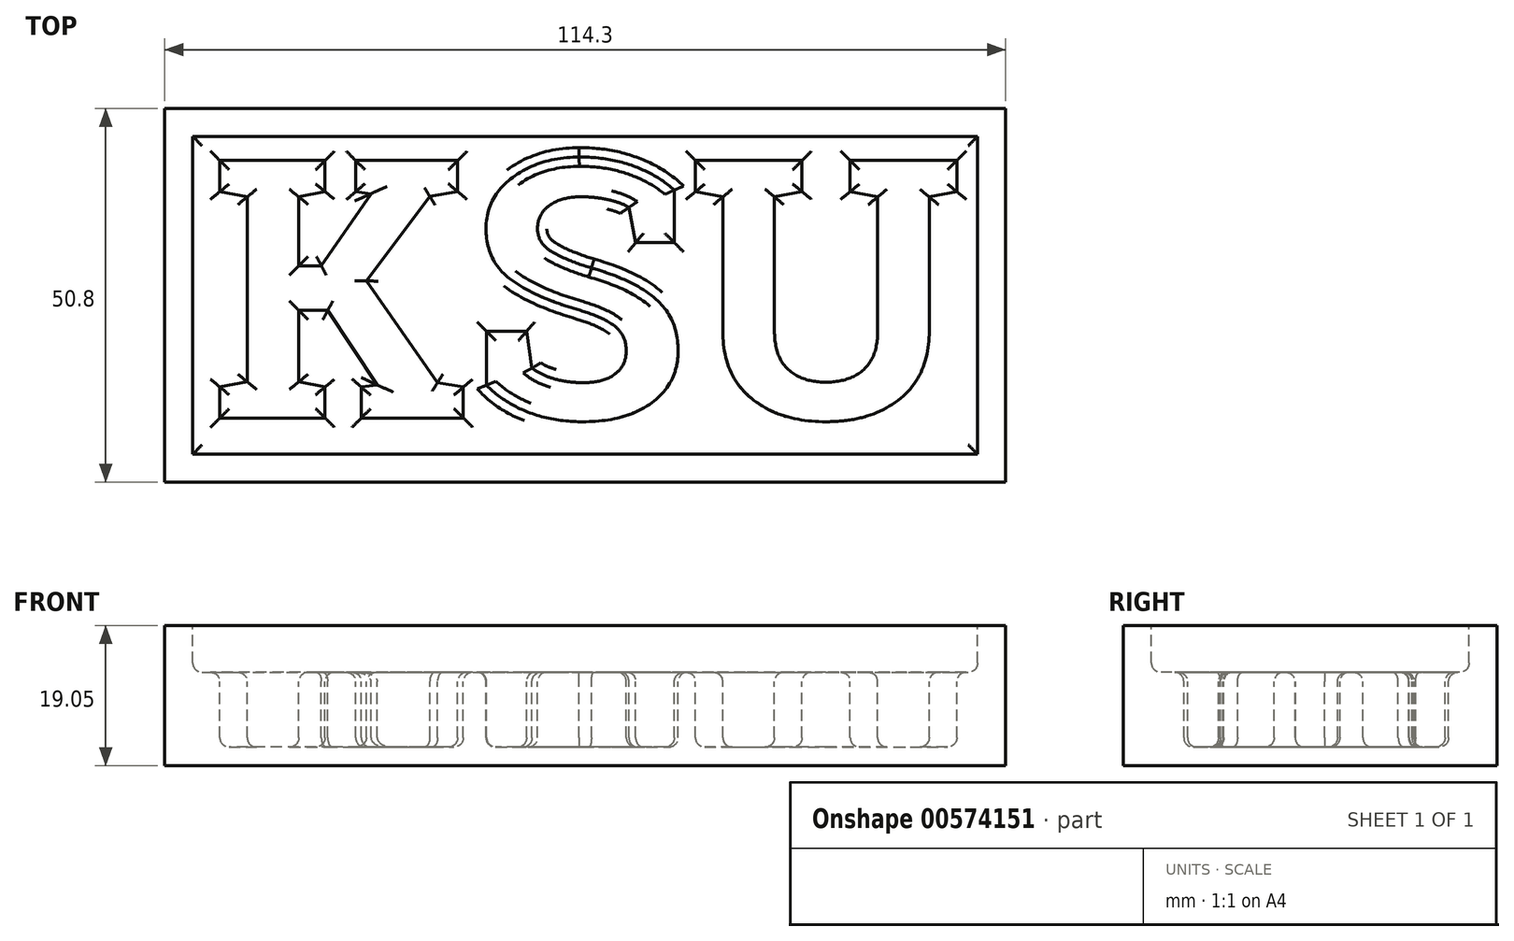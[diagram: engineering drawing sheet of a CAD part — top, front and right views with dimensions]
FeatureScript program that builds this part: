
annotation { "Feature Type Name" : "Feature", "Feature Type Description" : "" }
export const myFeature = defineFeature(function(context is Context, id is Id, definition is map)
    precondition{}
    {
        {
            var Q0;
            Q0=qCreatedBy(makeId("Top.planeOp"),FACE);
            var sketch = newSketch(context, id + "F0", { "sketchPlane" : qUnion([Q0])});
            skLineSegment(sketch, "E0.bottom", {"start": v(-40.64, 25.4) * mm, "end": v(73.66, 25.4) * mm});
            skLineSegment(sketch, "E0.top", {"start": v(-40.64, -25.4) * mm, "end": v(73.66, -25.4) * mm});
            skLineSegment(sketch, "E0.left", {"start": v(-40.64, 25.4) * mm, "end": v(-40.64, -25.4) * mm});
            skLineSegment(sketch, "E0.right", {"start": v(73.66, 25.4) * mm, "end": v(73.66, -25.4) * mm});
            skSolve(sketch);
        }
        {
            var Q0;
            Q0=makeQuery(id+"F0.imprint","IMPRINT",FACE,{"disambiguationData":[TD([[makeQuery(id+"F0.imprint","IMPRINT",EDGE,{"derivedFrom":sQuery(id+"F0.wireOp",EDGE,"E0.bottom")}),-1.0]])]});
            extrude(context, id + "F1", {"entities" : qUnion([Q0]), "depth" : 19.05 * mm, "offsetDistance" : 25.4 * mm});
        }
        {
            var Q0;
            Q0=makeQuery(id+"F1.opExtrude","CAP_FACE",FACE,{"disambiguationData":[OSD([sQuery(id+"F0.wireOp",EDGE,"E0.bottom"),sQuery(id+"F0.wireOp",EDGE,"E0.top"),sQuery(id+"F0.wireOp",EDGE,"E0.left"),sQuery(id+"F0.wireOp",EDGE,"E0.right")])],"isStart":false});
            var sketch = newSketch(context, id + "F2", { "sketchPlane" : qUnion([Q0])});
            skText(sketch, "E1", { "text": "KSU", "fontName": "RobotoSlab-Bold.ttf"});
            const initialGuessF2  = {"E1": [-0.0345, -0.01668, 1, 0, 0.03545]};
            skSetInitialGuess(sketch, initialGuessF2);
            skSolve(sketch);
        }
        {
            var Q0;
            Q0=makeQuery(id+"F2.imprint","IMPRINT",FACE,{"disambiguationData":[TD([[makeQuery(id+"F2.imprint","IMPRINT",EDGE,{"derivedFrom":sQuery(id+"F2.wireOp",EDGE,"E1.sketch_text.stroke-0")}),-1.0]])]});
            var Q1;
            Q1=makeQuery(id+"F2.imprint","IMPRINT",FACE,{"disambiguationData":[TD([[makeQuery(id+"F2.imprint","IMPRINT",EDGE,{"derivedFrom":sQuery(id+"F2.wireOp",EDGE,"E1.sketch_text.stroke-29")}),-1.0]])]});
            var Q2;
            Q2=makeQuery(id+"F2.imprint","IMPRINT",FACE,{"disambiguationData":[TD([[makeQuery(id+"F2.imprint","IMPRINT",EDGE,{"derivedFrom":sQuery(id+"F2.wireOp",EDGE,"E1.sketch_text.stroke-59")}),-1.0]])]});
            extrude(context, id + "F3", {"entities" : qUnion([Q0, Q1, Q2]), "operationType" : NewBodyOperationType.REMOVE, "oppositeDirection" : true, "depth" : 16.5 * mm, "offsetDistance" : 25.4 * mm});
        }
        {
            var Q0;
            Q0=makeQuery(id+"F1.opExtrude","CAP_FACE",FACE,{"disambiguationData":[OSD([sQuery(id+"F0.wireOp",EDGE,"E0.bottom"),sQuery(id+"F0.wireOp",EDGE,"E0.top"),sQuery(id+"F0.wireOp",EDGE,"E0.left"),sQuery(id+"F0.wireOp",EDGE,"E0.right")])],"isStart":false});
            var sketch = newSketch(context, id + "F4", { "sketchPlane" : qUnion([Q0])});
            skLineSegment(sketch, "E2.bottom", {"start": v(-36.83, 21.59) * mm, "end": v(69.85, 21.59) * mm});
            skLineSegment(sketch, "E2.top", {"start": v(-36.83, -21.59) * mm, "end": v(69.85, -21.59) * mm});
            skLineSegment(sketch, "E2.left", {"start": v(-36.83, 21.59) * mm, "end": v(-36.83, -21.59) * mm});
            skLineSegment(sketch, "E2.right", {"start": v(69.85, 21.59) * mm, "end": v(69.85, -21.59) * mm});
            skSolve(sketch);
        }
        {
            var Q0;
            Q0=makeQuery(id+"F4.imprint","IMPRINT",FACE,{"disambiguationData":[TD([[makeQuery(id+"F4.imprint","IMPRINT",EDGE,{"derivedFrom":sQuery(id+"F4.wireOp",EDGE,"E2.bottom")}),-1.0]])]});
            extrude(context, id + "F5", {"entities" : qUnion([Q0]), "operationType" : NewBodyOperationType.REMOVE, "oppositeDirection" : true, "depth" : 6.35 * mm, "offsetDistance" : 25.4 * mm});
        }
        {
            var Q0;
            Q0=makeQuery(id+"F3.boolean.opBoolean","COPY",FACE,{"derivedFrom":makeQuery(id+"F3.opExtrude","CAP_FACE",FACE,{"disambiguationData":[OSD([sQuery(id+"F2.wireOp",EDGE,"E1.sketch_text.stroke-0"),sQuery(id+"F2.wireOp",EDGE,"E1.sketch_text.stroke-1"),sQuery(id+"F2.wireOp",EDGE,"E1.sketch_text.stroke-2"),sQuery(id+"F2.wireOp",EDGE,"E1.sketch_text.stroke-3"),sQuery(id+"F2.wireOp",EDGE,"E1.sketch_text.stroke-4"),sQuery(id+"F2.wireOp",EDGE,"E1.sketch_text.stroke-5"),sQuery(id+"F2.wireOp",EDGE,"E1.sketch_text.stroke-6"),sQuery(id+"F2.wireOp",EDGE,"E1.sketch_text.stroke-7"),sQuery(id+"F2.wireOp",EDGE,"E1.sketch_text.stroke-8"),sQuery(id+"F2.wireOp",EDGE,"E1.sketch_text.stroke-9"),sQuery(id+"F2.wireOp",EDGE,"E1.sketch_text.stroke-10"),sQuery(id+"F2.wireOp",EDGE,"E1.sketch_text.stroke-11"),sQuery(id+"F2.wireOp",EDGE,"E1.sketch_text.stroke-12"),sQuery(id+"F2.wireOp",EDGE,"E1.sketch_text.stroke-13"),sQuery(id+"F2.wireOp",EDGE,"E1.sketch_text.stroke-14"),sQuery(id+"F2.wireOp",EDGE,"E1.sketch_text.stroke-15"),sQuery(id+"F2.wireOp",EDGE,"E1.sketch_text.stroke-16"),sQuery(id+"F2.wireOp",EDGE,"E1.sketch_text.stroke-17"),sQuery(id+"F2.wireOp",EDGE,"E1.sketch_text.stroke-18"),sQuery(id+"F2.wireOp",EDGE,"E1.sketch_text.stroke-19"),sQuery(id+"F2.wireOp",EDGE,"E1.sketch_text.stroke-20"),sQuery(id+"F2.wireOp",EDGE,"E1.sketch_text.stroke-21"),sQuery(id+"F2.wireOp",EDGE,"E1.sketch_text.stroke-22"),sQuery(id+"F2.wireOp",EDGE,"E1.sketch_text.stroke-23"),sQuery(id+"F2.wireOp",EDGE,"E1.sketch_text.stroke-24"),sQuery(id+"F2.wireOp",EDGE,"E1.sketch_text.stroke-25"),sQuery(id+"F2.wireOp",EDGE,"E1.sketch_text.stroke-26"),sQuery(id+"F2.wireOp",EDGE,"E1.sketch_text.stroke-27"),sQuery(id+"F2.wireOp",EDGE,"E1.sketch_text.stroke-28")])],"isStart":false})});
            var Q1;
            Q1=makeQuery(id+"F3.boolean.opBoolean","COPY",FACE,{"derivedFrom":makeQuery(id+"F3.opExtrude","CAP_FACE",FACE,{"disambiguationData":[OSD([sQuery(id+"F2.wireOp",EDGE,"E1.sketch_text.stroke-29"),sQuery(id+"F2.wireOp",EDGE,"E1.sketch_text.stroke-30"),sQuery(id+"F2.wireOp",EDGE,"E1.sketch_text.stroke-31"),sQuery(id+"F2.wireOp",EDGE,"E1.sketch_text.stroke-32"),sQuery(id+"F2.wireOp",EDGE,"E1.sketch_text.stroke-33"),sQuery(id+"F2.wireOp",EDGE,"E1.sketch_text.stroke-34"),sQuery(id+"F2.wireOp",EDGE,"E1.sketch_text.stroke-35"),sQuery(id+"F2.wireOp",EDGE,"E1.sketch_text.stroke-36"),sQuery(id+"F2.wireOp",EDGE,"E1.sketch_text.stroke-37"),sQuery(id+"F2.wireOp",EDGE,"E1.sketch_text.stroke-38"),sQuery(id+"F2.wireOp",EDGE,"E1.sketch_text.stroke-39"),sQuery(id+"F2.wireOp",EDGE,"E1.sketch_text.stroke-40"),sQuery(id+"F2.wireOp",EDGE,"E1.sketch_text.stroke-41"),sQuery(id+"F2.wireOp",EDGE,"E1.sketch_text.stroke-42"),sQuery(id+"F2.wireOp",EDGE,"E1.sketch_text.stroke-43"),sQuery(id+"F2.wireOp",EDGE,"E1.sketch_text.stroke-44"),sQuery(id+"F2.wireOp",EDGE,"E1.sketch_text.stroke-45"),sQuery(id+"F2.wireOp",EDGE,"E1.sketch_text.stroke-46"),sQuery(id+"F2.wireOp",EDGE,"E1.sketch_text.stroke-47"),sQuery(id+"F2.wireOp",EDGE,"E1.sketch_text.stroke-48"),sQuery(id+"F2.wireOp",EDGE,"E1.sketch_text.stroke-49"),sQuery(id+"F2.wireOp",EDGE,"E1.sketch_text.stroke-50"),sQuery(id+"F2.wireOp",EDGE,"E1.sketch_text.stroke-51"),sQuery(id+"F2.wireOp",EDGE,"E1.sketch_text.stroke-52"),sQuery(id+"F2.wireOp",EDGE,"E1.sketch_text.stroke-53"),sQuery(id+"F2.wireOp",EDGE,"E1.sketch_text.stroke-54"),sQuery(id+"F2.wireOp",EDGE,"E1.sketch_text.stroke-55"),sQuery(id+"F2.wireOp",EDGE,"E1.sketch_text.stroke-56"),sQuery(id+"F2.wireOp",EDGE,"E1.sketch_text.stroke-57"),sQuery(id+"F2.wireOp",EDGE,"E1.sketch_text.stroke-58")])],"isStart":false})});
            var Q2;
            Q2=makeQuery(id+"F3.boolean.opBoolean","COPY",FACE,{"derivedFrom":makeQuery(id+"F3.opExtrude","CAP_FACE",FACE,{"disambiguationData":[OSD([sQuery(id+"F2.wireOp",EDGE,"E1.sketch_text.stroke-59"),sQuery(id+"F2.wireOp",EDGE,"E1.sketch_text.stroke-60"),sQuery(id+"F2.wireOp",EDGE,"E1.sketch_text.stroke-61"),sQuery(id+"F2.wireOp",EDGE,"E1.sketch_text.stroke-62"),sQuery(id+"F2.wireOp",EDGE,"E1.sketch_text.stroke-63"),sQuery(id+"F2.wireOp",EDGE,"E1.sketch_text.stroke-64"),sQuery(id+"F2.wireOp",EDGE,"E1.sketch_text.stroke-65"),sQuery(id+"F2.wireOp",EDGE,"E1.sketch_text.stroke-66"),sQuery(id+"F2.wireOp",EDGE,"E1.sketch_text.stroke-67"),sQuery(id+"F2.wireOp",EDGE,"E1.sketch_text.stroke-68"),sQuery(id+"F2.wireOp",EDGE,"E1.sketch_text.stroke-69"),sQuery(id+"F2.wireOp",EDGE,"E1.sketch_text.stroke-70"),sQuery(id+"F2.wireOp",EDGE,"E1.sketch_text.stroke-71"),sQuery(id+"F2.wireOp",EDGE,"E1.sketch_text.stroke-72"),sQuery(id+"F2.wireOp",EDGE,"E1.sketch_text.stroke-73"),sQuery(id+"F2.wireOp",EDGE,"E1.sketch_text.stroke-74"),sQuery(id+"F2.wireOp",EDGE,"E1.sketch_text.stroke-75"),sQuery(id+"F2.wireOp",EDGE,"E1.sketch_text.stroke-76"),sQuery(id+"F2.wireOp",EDGE,"E1.sketch_text.stroke-77"),sQuery(id+"F2.wireOp",EDGE,"E1.sketch_text.stroke-78"),sQuery(id+"F2.wireOp",EDGE,"E1.sketch_text.stroke-79"),sQuery(id+"F2.wireOp",EDGE,"E1.sketch_text.stroke-80"),sQuery(id+"F2.wireOp",EDGE,"E1.sketch_text.stroke-81"),sQuery(id+"F2.wireOp",EDGE,"E1.sketch_text.stroke-82")])],"isStart":false})});
            fillet(context, id + "F6", {"entities" : qUnion([Q0, Q1, Q2]), "radius" : 1.27 * mm, "tangentPropagation" : true, "allowEdgeOverflow" : false});
        }
        {
            var Q0;
            Q0=makeQuery(id+"F5.boolean.opBoolean","COPY",FACE,{"derivedFrom":makeQuery(id+"F5.opExtrude","CAP_FACE",FACE,{"disambiguationData":[OSD([sQuery(id+"F2.wireOp",EDGE,"E1.sketch_text.stroke-0"),sQuery(id+"F2.wireOp",EDGE,"E1.sketch_text.stroke-1"),sQuery(id+"F2.wireOp",EDGE,"E1.sketch_text.stroke-2"),sQuery(id+"F2.wireOp",EDGE,"E1.sketch_text.stroke-3"),sQuery(id+"F2.wireOp",EDGE,"E1.sketch_text.stroke-4"),sQuery(id+"F2.wireOp",EDGE,"E1.sketch_text.stroke-5"),sQuery(id+"F2.wireOp",EDGE,"E1.sketch_text.stroke-6"),sQuery(id+"F2.wireOp",EDGE,"E1.sketch_text.stroke-7"),sQuery(id+"F2.wireOp",EDGE,"E1.sketch_text.stroke-8"),sQuery(id+"F2.wireOp",EDGE,"E1.sketch_text.stroke-9"),sQuery(id+"F2.wireOp",EDGE,"E1.sketch_text.stroke-10"),sQuery(id+"F2.wireOp",EDGE,"E1.sketch_text.stroke-11"),sQuery(id+"F2.wireOp",EDGE,"E1.sketch_text.stroke-12"),sQuery(id+"F2.wireOp",EDGE,"E1.sketch_text.stroke-13"),sQuery(id+"F2.wireOp",EDGE,"E1.sketch_text.stroke-14"),sQuery(id+"F2.wireOp",EDGE,"E1.sketch_text.stroke-15"),sQuery(id+"F2.wireOp",EDGE,"E1.sketch_text.stroke-16"),sQuery(id+"F2.wireOp",EDGE,"E1.sketch_text.stroke-17"),sQuery(id+"F2.wireOp",EDGE,"E1.sketch_text.stroke-18"),sQuery(id+"F2.wireOp",EDGE,"E1.sketch_text.stroke-19"),sQuery(id+"F2.wireOp",EDGE,"E1.sketch_text.stroke-20"),sQuery(id+"F2.wireOp",EDGE,"E1.sketch_text.stroke-21"),sQuery(id+"F2.wireOp",EDGE,"E1.sketch_text.stroke-22"),sQuery(id+"F2.wireOp",EDGE,"E1.sketch_text.stroke-23"),sQuery(id+"F2.wireOp",EDGE,"E1.sketch_text.stroke-24"),sQuery(id+"F2.wireOp",EDGE,"E1.sketch_text.stroke-25"),sQuery(id+"F2.wireOp",EDGE,"E1.sketch_text.stroke-26"),sQuery(id+"F2.wireOp",EDGE,"E1.sketch_text.stroke-27"),sQuery(id+"F2.wireOp",EDGE,"E1.sketch_text.stroke-28"),sQuery(id+"F2.wireOp",EDGE,"E1.sketch_text.stroke-29"),sQuery(id+"F2.wireOp",EDGE,"E1.sketch_text.stroke-30"),sQuery(id+"F2.wireOp",EDGE,"E1.sketch_text.stroke-31"),sQuery(id+"F2.wireOp",EDGE,"E1.sketch_text.stroke-32"),sQuery(id+"F2.wireOp",EDGE,"E1.sketch_text.stroke-33"),sQuery(id+"F2.wireOp",EDGE,"E1.sketch_text.stroke-34"),sQuery(id+"F2.wireOp",EDGE,"E1.sketch_text.stroke-35"),sQuery(id+"F2.wireOp",EDGE,"E1.sketch_text.stroke-36"),sQuery(id+"F2.wireOp",EDGE,"E1.sketch_text.stroke-37"),sQuery(id+"F2.wireOp",EDGE,"E1.sketch_text.stroke-38"),sQuery(id+"F2.wireOp",EDGE,"E1.sketch_text.stroke-39"),sQuery(id+"F2.wireOp",EDGE,"E1.sketch_text.stroke-40"),sQuery(id+"F2.wireOp",EDGE,"E1.sketch_text.stroke-41"),sQuery(id+"F2.wireOp",EDGE,"E1.sketch_text.stroke-42"),sQuery(id+"F2.wireOp",EDGE,"E1.sketch_text.stroke-43"),sQuery(id+"F2.wireOp",EDGE,"E1.sketch_text.stroke-44"),sQuery(id+"F2.wireOp",EDGE,"E1.sketch_text.stroke-45"),sQuery(id+"F2.wireOp",EDGE,"E1.sketch_text.stroke-46"),sQuery(id+"F2.wireOp",EDGE,"E1.sketch_text.stroke-47"),sQuery(id+"F2.wireOp",EDGE,"E1.sketch_text.stroke-48"),sQuery(id+"F2.wireOp",EDGE,"E1.sketch_text.stroke-49"),sQuery(id+"F2.wireOp",EDGE,"E1.sketch_text.stroke-50"),sQuery(id+"F2.wireOp",EDGE,"E1.sketch_text.stroke-51"),sQuery(id+"F2.wireOp",EDGE,"E1.sketch_text.stroke-52"),sQuery(id+"F2.wireOp",EDGE,"E1.sketch_text.stroke-53"),sQuery(id+"F2.wireOp",EDGE,"E1.sketch_text.stroke-54"),sQuery(id+"F2.wireOp",EDGE,"E1.sketch_text.stroke-55"),sQuery(id+"F2.wireOp",EDGE,"E1.sketch_text.stroke-56"),sQuery(id+"F2.wireOp",EDGE,"E1.sketch_text.stroke-57"),sQuery(id+"F2.wireOp",EDGE,"E1.sketch_text.stroke-58"),sQuery(id+"F2.wireOp",EDGE,"E1.sketch_text.stroke-59"),sQuery(id+"F2.wireOp",EDGE,"E1.sketch_text.stroke-60"),sQuery(id+"F2.wireOp",EDGE,"E1.sketch_text.stroke-61"),sQuery(id+"F2.wireOp",EDGE,"E1.sketch_text.stroke-62"),sQuery(id+"F2.wireOp",EDGE,"E1.sketch_text.stroke-63"),sQuery(id+"F2.wireOp",EDGE,"E1.sketch_text.stroke-64"),sQuery(id+"F2.wireOp",EDGE,"E1.sketch_text.stroke-65"),sQuery(id+"F2.wireOp",EDGE,"E1.sketch_text.stroke-66"),sQuery(id+"F2.wireOp",EDGE,"E1.sketch_text.stroke-67"),sQuery(id+"F2.wireOp",EDGE,"E1.sketch_text.stroke-68"),sQuery(id+"F2.wireOp",EDGE,"E1.sketch_text.stroke-69"),sQuery(id+"F2.wireOp",EDGE,"E1.sketch_text.stroke-70"),sQuery(id+"F2.wireOp",EDGE,"E1.sketch_text.stroke-71"),sQuery(id+"F2.wireOp",EDGE,"E1.sketch_text.stroke-72"),sQuery(id+"F2.wireOp",EDGE,"E1.sketch_text.stroke-73"),sQuery(id+"F2.wireOp",EDGE,"E1.sketch_text.stroke-74"),sQuery(id+"F2.wireOp",EDGE,"E1.sketch_text.stroke-75"),sQuery(id+"F2.wireOp",EDGE,"E1.sketch_text.stroke-76"),sQuery(id+"F2.wireOp",EDGE,"E1.sketch_text.stroke-77"),sQuery(id+"F2.wireOp",EDGE,"E1.sketch_text.stroke-78"),sQuery(id+"F2.wireOp",EDGE,"E1.sketch_text.stroke-79"),sQuery(id+"F2.wireOp",EDGE,"E1.sketch_text.stroke-80"),sQuery(id+"F2.wireOp",EDGE,"E1.sketch_text.stroke-81"),sQuery(id+"F2.wireOp",EDGE,"E1.sketch_text.stroke-82"),sQuery(id+"F4.wireOp",EDGE,"E2.bottom"),sQuery(id+"F4.wireOp",EDGE,"E2.top"),sQuery(id+"F4.wireOp",EDGE,"E2.left"),sQuery(id+"F4.wireOp",EDGE,"E2.right")])],"isStart":false})});
            fillet(context, id + "F7", {"entities" : qUnion([Q0]), "radius" : 1.27 * mm, "tangentPropagation" : true, "allowEdgeOverflow" : false});
        }
    });
